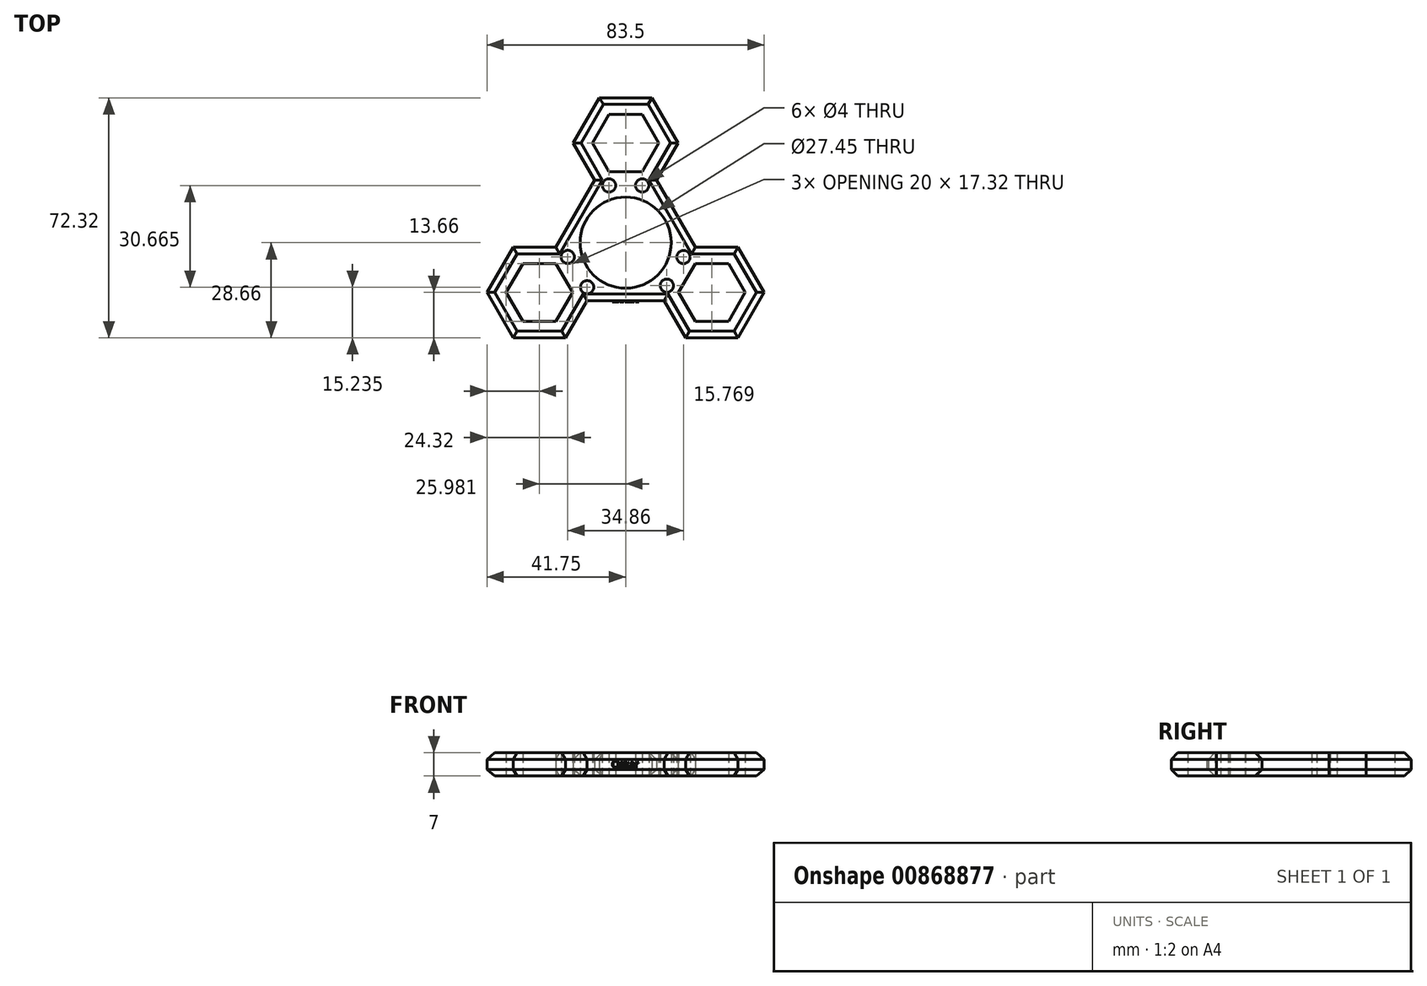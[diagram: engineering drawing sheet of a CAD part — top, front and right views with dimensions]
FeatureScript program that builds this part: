
annotation { "Feature Type Name" : "Feature", "Feature Type Description" : "" }
export const myFeature = defineFeature(function(context is Context, id is Id, definition is map)
    precondition{}
    {
        {
            var Q0;
            Q0=qCreatedBy(makeId("Top.planeOp"),FACE);
            var sketch = newSketch(context, id + "F0", { "sketchPlane" : qUnion([Q0])});
            skCircle(sketch, "E0", {"center": v(0, 0) * mm, "radius": 13.73 * mm});
            skCircle(sketch, "E1.cCircle", {"center": v(-25.98, -15) * mm, "radius": 8.66 * mm, "construction": true});
            skLineSegment(sketch, "E1.0", {"start": v(-20.98, -6.34) * mm, "end": v(-15.98, -15) * mm});
            skLineSegment(sketch, "E1.1", {"start": v(-15.98, -15) * mm, "end": v(-20.98, -23.66) * mm});
            skLineSegment(sketch, "E1.2", {"start": v(-20.98, -23.66) * mm, "end": v(-30.98, -23.66) * mm});
            skLineSegment(sketch, "E1.3", {"start": v(-30.98, -23.66) * mm, "end": v(-35.98, -15) * mm});
            skLineSegment(sketch, "E1.4", {"start": v(-35.98, -15) * mm, "end": v(-30.98, -6.34) * mm});
            skLineSegment(sketch, "E1.5", {"start": v(-30.98, -6.34) * mm, "end": v(-20.98, -6.34) * mm});
            skCircle(sketch, "E2.cCircle", {"center": v(25.98, -15) * mm, "radius": 8.66 * mm, "construction": true});
            skLineSegment(sketch, "E2.0", {"start": v(15.98, -15) * mm, "end": v(20.98, -6.34) * mm});
            skLineSegment(sketch, "E2.1", {"start": v(20.98, -6.34) * mm, "end": v(30.98, -6.34) * mm});
            skLineSegment(sketch, "E2.2", {"start": v(30.98, -6.34) * mm, "end": v(35.98, -15) * mm});
            skLineSegment(sketch, "E2.3", {"start": v(35.98, -15) * mm, "end": v(30.98, -23.66) * mm});
            skLineSegment(sketch, "E2.4", {"start": v(30.98, -23.66) * mm, "end": v(20.98, -23.66) * mm});
            skLineSegment(sketch, "E2.5", {"start": v(20.98, -23.66) * mm, "end": v(15.98, -15) * mm});
            skCircle(sketch, "E3.cCircle", {"center": v(0, 30) * mm, "radius": 8.66 * mm, "construction": true});
            skLineSegment(sketch, "E3.0", {"start": v(5, 21.34) * mm, "end": v(-5, 21.34) * mm});
            skLineSegment(sketch, "E3.1", {"start": v(-5, 21.34) * mm, "end": v(-10, 30) * mm});
            skLineSegment(sketch, "E3.2", {"start": v(-10, 30) * mm, "end": v(-5, 38.66) * mm});
            skLineSegment(sketch, "E3.3", {"start": v(-5, 38.66) * mm, "end": v(5, 38.66) * mm});
            skLineSegment(sketch, "E3.4", {"start": v(5, 38.66) * mm, "end": v(10, 30) * mm});
            skLineSegment(sketch, "E3.5", {"start": v(10, 30) * mm, "end": v(5, 21.34) * mm});
            skLineSegment(sketch, "E4.0", {"start": v(-5, 43.66) * mm, "end": v(5, 43.66) * mm});
            skLineSegment(sketch, "E5.0", {"start": v(-14.33, 32.5) * mm, "end": v(-9.33, 41.16) * mm});
            skLineSegment(sketch, "E6.0", {"start": v(9.33, 41.16) * mm, "end": v(14.33, 32.5) * mm});
            skLineSegment(sketch, "E7.0", {"start": v(-9.33, 18.84) * mm, "end": v(-14.33, 27.5) * mm});
            skLineSegment(sketch, "E8.0", {"start": v(14.33, 27.5) * mm, "end": v(9.33, 18.84) * mm});
            skLineSegment(sketch, "E9.0", {"start": v(-30.98, -1.34) * mm, "end": v(-20.98, -1.34) * mm});
            skLineSegment(sketch, "E10.0", {"start": v(-40.31, -12.5) * mm, "end": v(-35.31, -3.84) * mm});
            skLineSegment(sketch, "E11.0", {"start": v(-35.31, -26.16) * mm, "end": v(-40.31, -17.5) * mm});
            skLineSegment(sketch, "E12.0", {"start": v(-20.98, -28.66) * mm, "end": v(-30.98, -28.66) * mm});
            skLineSegment(sketch, "E13.0", {"start": v(-11.65, -17.5) * mm, "end": v(-16.65, -26.16) * mm});
            skLineSegment(sketch, "E14.0", {"start": v(16.65, -26.16) * mm, "end": v(11.65, -17.5) * mm});
            skLineSegment(sketch, "E15.0", {"start": v(30.98, -28.66) * mm, "end": v(20.98, -28.66) * mm});
            skLineSegment(sketch, "E16.0", {"start": v(40.3, -17.5) * mm, "end": v(35.31, -26.16) * mm});
            skLineSegment(sketch, "E17.0", {"start": v(35.31, -3.84) * mm, "end": v(40.31, -12.5) * mm});
            skLineSegment(sketch, "E18.0", {"start": v(20.98, -1.34) * mm, "end": v(30.98, -1.34) * mm});
            skLineSegment(sketch, "E19", {"start": v(14.33, 27.5) * mm, "end": v(15.77, 30) * mm});
            skLineSegment(sketch, "E20", {"start": v(14.33, 32.5) * mm, "end": v(15.77, 30) * mm});
            skLineSegment(sketch, "E21", {"start": v(-14.33, 27.5) * mm, "end": v(-15.77, 30) * mm});
            skLineSegment(sketch, "E22", {"start": v(-14.33, 32.5) * mm, "end": v(-15.77, 30) * mm});
            skLineSegment(sketch, "E23", {"start": v(-5, 43.66) * mm, "end": v(-7.89, 43.66) * mm});
            skLineSegment(sketch, "E24", {"start": v(5, 43.66) * mm, "end": v(7.89, 43.66) * mm});
            skLineSegment(sketch, "E25", {"start": v(-9.33, 41.16) * mm, "end": v(-7.89, 43.66) * mm});
            skLineSegment(sketch, "E26", {"start": v(9.33, 41.16) * mm, "end": v(7.89, 43.66) * mm});
            skLineSegment(sketch, "E27", {"start": v(30.98, -1.34) * mm, "end": v(33.87, -1.34) * mm});
            skLineSegment(sketch, "E28", {"start": v(35.31, -3.84) * mm, "end": v(33.87, -1.34) * mm});
            skLineSegment(sketch, "E29", {"start": v(40.31, -12.5) * mm, "end": v(41.75, -15) * mm});
            skLineSegment(sketch, "E30", {"start": v(40.3, -17.5) * mm, "end": v(41.75, -15) * mm});
            skLineSegment(sketch, "E31", {"start": v(35.31, -26.16) * mm, "end": v(33.87, -28.66) * mm});
            skLineSegment(sketch, "E32", {"start": v(16.65, -26.16) * mm, "end": v(18.1, -28.66) * mm});
            skLineSegment(sketch, "E33", {"start": v(30.98, -28.66) * mm, "end": v(33.87, -28.66) * mm});
            skLineSegment(sketch, "E34", {"start": v(20.98, -28.66) * mm, "end": v(18.1, -28.66) * mm});
            skLineSegment(sketch, "E35", {"start": v(-30.98, -1.34) * mm, "end": v(-33.87, -1.34) * mm});
            skLineSegment(sketch, "E36", {"start": v(-35.31, -3.84) * mm, "end": v(-33.87, -1.34) * mm});
            skLineSegment(sketch, "E37", {"start": v(-40.31, -12.5) * mm, "end": v(-41.75, -15) * mm});
            skLineSegment(sketch, "E38", {"start": v(-40.31, -17.5) * mm, "end": v(-41.75, -15) * mm});
            skLineSegment(sketch, "E39", {"start": v(-35.31, -26.16) * mm, "end": v(-33.87, -28.66) * mm});
            skLineSegment(sketch, "E40", {"start": v(-30.98, -28.66) * mm, "end": v(-33.87, -28.66) * mm});
            skLineSegment(sketch, "E41", {"start": v(-20.98, -28.66) * mm, "end": v(-18.1, -28.66) * mm});
            skLineSegment(sketch, "E42", {"start": v(-16.65, -26.16) * mm, "end": v(-18.1, -28.66) * mm});
            skLineSegment(sketch, "E43", {"start": v(-20.98, -1.34) * mm, "end": v(-9.33, 18.84) * mm});
            skLineSegment(sketch, "E44", {"start": v(9.33, 18.84) * mm, "end": v(20.98, -1.34) * mm});
            skLineSegment(sketch, "E45", {"start": v(-11.65, -17.5) * mm, "end": v(11.65, -17.5) * mm});
            skCircle(sketch, "E46", {"center": v(-5, 17.24) * mm, "radius": 2 * mm});
            skCircle(sketch, "E47", {"center": v(5, 17.24) * mm, "radius": 2 * mm});
            skCircle(sketch, "E48", {"center": v(-17.43, -4.29) * mm, "radius": 2 * mm});
            skCircle(sketch, "E49", {"center": v(-11.6, -13.42) * mm, "radius": 2 * mm});
            skCircle(sketch, "E50", {"center": v(12.43, -12.95) * mm, "radius": 2 * mm});
            skCircle(sketch, "E51", {"center": v(17.43, -4.34) * mm, "radius": 2 * mm});
            skSolve(sketch);
        }
        {
            var Q0;
            Q0=makeQuery(id+"F0.imprint","IMPRINT",FACE,{"disambiguationData":[TD([[makeQuery(id+"F0.imprint","IMPRINT",EDGE,{"derivedFrom":sQuery(id+"F0.wireOp",EDGE,"E0")}),-1.0]])]});
            extrude(context, id + "F1", {"entities" : qUnion([Q0]), "depth" : 7 * mm, "offsetDistance" : 25 * mm});
        }
        {
            var Q0;
            Q0=makeQuery(id+"F1.opExtrude","CAP_EDGE",EDGE,{"disambiguationData":[OSD([sQuery(id+"F0.wireOp",EDGE,"E5.0"),sQuery(id+"F0.wireOp",EDGE,"E22"),sQuery(id+"F0.wireOp",EDGE,"E25")])],"isStart":false});
            var Q1;
            Q1=makeQuery(id+"F1.opExtrude","CAP_EDGE",EDGE,{"disambiguationData":[OSD([sQuery(id+"F0.wireOp",EDGE,"E4.0"),sQuery(id+"F0.wireOp",EDGE,"E23"),sQuery(id+"F0.wireOp",EDGE,"E24")])],"isStart":false});
            var Q2;
            Q2=makeQuery(id+"F1.opExtrude","CAP_EDGE",EDGE,{"disambiguationData":[OSD([sQuery(id+"F0.wireOp",EDGE,"E7.0"),sQuery(id+"F0.wireOp",EDGE,"E21")])],"isStart":false});
            var Q3;
            Q3=makeQuery(id+"F1.opExtrude","CAP_EDGE",EDGE,{"disambiguationData":[OSD([sQuery(id+"F0.wireOp",EDGE,"E6.0"),sQuery(id+"F0.wireOp",EDGE,"E20"),sQuery(id+"F0.wireOp",EDGE,"E26")])],"isStart":false});
            var Q4;
            Q4=makeQuery(id+"F1.opExtrude","CAP_EDGE",EDGE,{"disambiguationData":[OSD([sQuery(id+"F0.wireOp",EDGE,"E8.0"),sQuery(id+"F0.wireOp",EDGE,"E19")])],"isStart":false});
            var Q5;
            Q5=makeQuery(id+"F1.opExtrude","CAP_EDGE",EDGE,{"disambiguationData":[OSD([sQuery(id+"F0.wireOp",EDGE,"E44")])],"isStart":false});
            var Q6;
            Q6=makeQuery(id+"F1.opExtrude","CAP_EDGE",EDGE,{"disambiguationData":[OSD([sQuery(id+"F0.wireOp",EDGE,"E18.0"),sQuery(id+"F0.wireOp",EDGE,"E27")])],"isStart":false});
            var Q7;
            Q7=makeQuery(id+"F1.opExtrude","CAP_EDGE",EDGE,{"disambiguationData":[OSD([sQuery(id+"F0.wireOp",EDGE,"E17.0"),sQuery(id+"F0.wireOp",EDGE,"E28"),sQuery(id+"F0.wireOp",EDGE,"E29")])],"isStart":false});
            var Q8;
            Q8=makeQuery(id+"F1.opExtrude","CAP_EDGE",EDGE,{"disambiguationData":[OSD([sQuery(id+"F0.wireOp",EDGE,"E16.0"),sQuery(id+"F0.wireOp",EDGE,"E30"),sQuery(id+"F0.wireOp",EDGE,"E31")])],"isStart":false});
            var Q9;
            Q9=makeQuery(id+"F1.opExtrude","CAP_EDGE",EDGE,{"disambiguationData":[OSD([sQuery(id+"F0.wireOp",EDGE,"E15.0"),sQuery(id+"F0.wireOp",EDGE,"E33"),sQuery(id+"F0.wireOp",EDGE,"E34")])],"isStart":false});
            var Q10;
            Q10=makeQuery(id+"F1.opExtrude","CAP_EDGE",EDGE,{"disambiguationData":[OSD([sQuery(id+"F0.wireOp",EDGE,"E14.0"),sQuery(id+"F0.wireOp",EDGE,"E32")])],"isStart":false});
            var Q11;
            Q11=makeQuery(id+"F1.opExtrude","CAP_EDGE",EDGE,{"disambiguationData":[OSD([sQuery(id+"F0.wireOp",EDGE,"E45")])],"isStart":false});
            var Q12;
            Q12=makeQuery(id+"F1.opExtrude","CAP_EDGE",EDGE,{"disambiguationData":[OSD([sQuery(id+"F0.wireOp",EDGE,"E13.0"),sQuery(id+"F0.wireOp",EDGE,"E42")])],"isStart":false});
            var Q13;
            Q13=makeQuery(id+"F1.opExtrude","CAP_EDGE",EDGE,{"disambiguationData":[OSD([sQuery(id+"F0.wireOp",EDGE,"E12.0"),sQuery(id+"F0.wireOp",EDGE,"E40"),sQuery(id+"F0.wireOp",EDGE,"E41")])],"isStart":false});
            var Q14;
            Q14=makeQuery(id+"F1.opExtrude","CAP_EDGE",EDGE,{"disambiguationData":[OSD([sQuery(id+"F0.wireOp",EDGE,"E11.0"),sQuery(id+"F0.wireOp",EDGE,"E38"),sQuery(id+"F0.wireOp",EDGE,"E39")])],"isStart":false});
            var Q15;
            Q15=makeQuery(id+"F1.opExtrude","CAP_EDGE",EDGE,{"disambiguationData":[OSD([sQuery(id+"F0.wireOp",EDGE,"E10.0"),sQuery(id+"F0.wireOp",EDGE,"E36"),sQuery(id+"F0.wireOp",EDGE,"E37")])],"isStart":false});
            var Q16;
            Q16=makeQuery(id+"F1.opExtrude","CAP_EDGE",EDGE,{"disambiguationData":[OSD([sQuery(id+"F0.wireOp",EDGE,"E9.0"),sQuery(id+"F0.wireOp",EDGE,"E35")])],"isStart":false});
            var Q17;
            Q17=makeQuery(id+"F1.opExtrude","CAP_EDGE",EDGE,{"disambiguationData":[OSD([sQuery(id+"F0.wireOp",EDGE,"E43")])],"isStart":false});
            var Q18;
            Q18=makeQuery(id+"F1.opExtrude","CAP_EDGE",EDGE,{"disambiguationData":[OSD([sQuery(id+"F0.wireOp",EDGE,"E9.0"),sQuery(id+"F0.wireOp",EDGE,"E35")])],"isStart":true});
            var Q19;
            Q19=makeQuery(id+"F1.opExtrude","CAP_EDGE",EDGE,{"disambiguationData":[OSD([sQuery(id+"F0.wireOp",EDGE,"E10.0"),sQuery(id+"F0.wireOp",EDGE,"E36"),sQuery(id+"F0.wireOp",EDGE,"E37")])],"isStart":true});
            var Q20;
            Q20=makeQuery(id+"F1.opExtrude","CAP_EDGE",EDGE,{"disambiguationData":[OSD([sQuery(id+"F0.wireOp",EDGE,"E11.0"),sQuery(id+"F0.wireOp",EDGE,"E38"),sQuery(id+"F0.wireOp",EDGE,"E39")])],"isStart":true});
            var Q21;
            Q21=makeQuery(id+"F1.opExtrude","CAP_EDGE",EDGE,{"disambiguationData":[OSD([sQuery(id+"F0.wireOp",EDGE,"E12.0"),sQuery(id+"F0.wireOp",EDGE,"E40"),sQuery(id+"F0.wireOp",EDGE,"E41")])],"isStart":true});
            var Q22;
            Q22=makeQuery(id+"F1.opExtrude","CAP_EDGE",EDGE,{"disambiguationData":[OSD([sQuery(id+"F0.wireOp",EDGE,"E13.0"),sQuery(id+"F0.wireOp",EDGE,"E42")])],"isStart":true});
            var Q23;
            Q23=makeQuery(id+"F1.opExtrude","CAP_EDGE",EDGE,{"disambiguationData":[OSD([sQuery(id+"F0.wireOp",EDGE,"E45")])],"isStart":true});
            var Q24;
            Q24=makeQuery(id+"F1.opExtrude","CAP_EDGE",EDGE,{"disambiguationData":[OSD([sQuery(id+"F0.wireOp",EDGE,"E14.0"),sQuery(id+"F0.wireOp",EDGE,"E32")])],"isStart":true});
            var Q25;
            Q25=makeQuery(id+"F1.opExtrude","CAP_EDGE",EDGE,{"disambiguationData":[OSD([sQuery(id+"F0.wireOp",EDGE,"E15.0"),sQuery(id+"F0.wireOp",EDGE,"E33"),sQuery(id+"F0.wireOp",EDGE,"E34")])],"isStart":true});
            var Q26;
            Q26=makeQuery(id+"F1.opExtrude","CAP_EDGE",EDGE,{"disambiguationData":[OSD([sQuery(id+"F0.wireOp",EDGE,"E16.0"),sQuery(id+"F0.wireOp",EDGE,"E30"),sQuery(id+"F0.wireOp",EDGE,"E31")])],"isStart":true});
            var Q27;
            Q27=makeQuery(id+"F1.opExtrude","CAP_EDGE",EDGE,{"disambiguationData":[OSD([sQuery(id+"F0.wireOp",EDGE,"E17.0"),sQuery(id+"F0.wireOp",EDGE,"E28"),sQuery(id+"F0.wireOp",EDGE,"E29")])],"isStart":true});
            var Q28;
            Q28=makeQuery(id+"F1.opExtrude","CAP_EDGE",EDGE,{"disambiguationData":[OSD([sQuery(id+"F0.wireOp",EDGE,"E18.0"),sQuery(id+"F0.wireOp",EDGE,"E27")])],"isStart":true});
            var Q29;
            Q29=makeQuery(id+"F1.opExtrude","CAP_EDGE",EDGE,{"disambiguationData":[OSD([sQuery(id+"F0.wireOp",EDGE,"E44")])],"isStart":true});
            var Q30;
            Q30=makeQuery(id+"F1.opExtrude","CAP_EDGE",EDGE,{"disambiguationData":[OSD([sQuery(id+"F0.wireOp",EDGE,"E8.0"),sQuery(id+"F0.wireOp",EDGE,"E19")])],"isStart":true});
            var Q31;
            Q31=makeQuery(id+"F1.opExtrude","CAP_EDGE",EDGE,{"disambiguationData":[OSD([sQuery(id+"F0.wireOp",EDGE,"E6.0"),sQuery(id+"F0.wireOp",EDGE,"E20"),sQuery(id+"F0.wireOp",EDGE,"E26")])],"isStart":true});
            var Q32;
            Q32=makeQuery(id+"F1.opExtrude","CAP_EDGE",EDGE,{"disambiguationData":[OSD([sQuery(id+"F0.wireOp",EDGE,"E4.0"),sQuery(id+"F0.wireOp",EDGE,"E23"),sQuery(id+"F0.wireOp",EDGE,"E24")])],"isStart":true});
            var Q33;
            Q33=makeQuery(id+"F1.opExtrude","CAP_EDGE",EDGE,{"disambiguationData":[OSD([sQuery(id+"F0.wireOp",EDGE,"E5.0"),sQuery(id+"F0.wireOp",EDGE,"E22"),sQuery(id+"F0.wireOp",EDGE,"E25")])],"isStart":true});
            var Q34;
            Q34=makeQuery(id+"F1.opExtrude","CAP_EDGE",EDGE,{"disambiguationData":[OSD([sQuery(id+"F0.wireOp",EDGE,"E7.0"),sQuery(id+"F0.wireOp",EDGE,"E21")])],"isStart":true});
            var Q35;
            Q35=makeQuery(id+"F1.opExtrude","CAP_EDGE",EDGE,{"disambiguationData":[OSD([sQuery(id+"F0.wireOp",EDGE,"E43")])],"isStart":true});
            chamfer(context, id + "F2", {"entities" : qUnion([Q0, Q1, Q2, Q3, Q4, Q5, Q6, Q7, Q8, Q9, Q10, Q11, Q12, Q13, Q14, Q15, Q16, Q17, Q18, Q19, Q20, Q21, Q22, Q23, Q24, Q25, Q26, Q27, Q28, Q29, Q30, Q31, Q32, Q33, Q34, Q35]), "width" : 2 * mm, "tangentPropagation" : true});
        }
        {
            var Q0;
            Q0=makeQuery(id+"F1.opExtrude","SWEPT_FACE",FACE,{"disambiguationData":[OSD([sQuery(id+"F0.wireOp",EDGE,"E45")])]});
            var sketch = newSketch(context, id + "F3", { "sketchPlane" : qUnion([Q0])});
            skText(sketch, "E52", { "text": "Oskar", "fontName": "OpenSans-Regular.ttf"});
            const initialGuessF3  = {"E52": [-0.0042, 0.00247, 1, 0, 0.00215]};
            skSetInitialGuess(sketch, initialGuessF3);
            skSolve(sketch);
        }
        {
            var Q0;
            Q0 = qSketchRegion(id + "F3", true);
            extrude(context, id + "F4", {"entities" : qUnion([Q0]), "operationType" : NewBodyOperationType.ADD, "depth" : 0.33 * mm, "offsetDistance" : 25 * mm});
        }
    });
